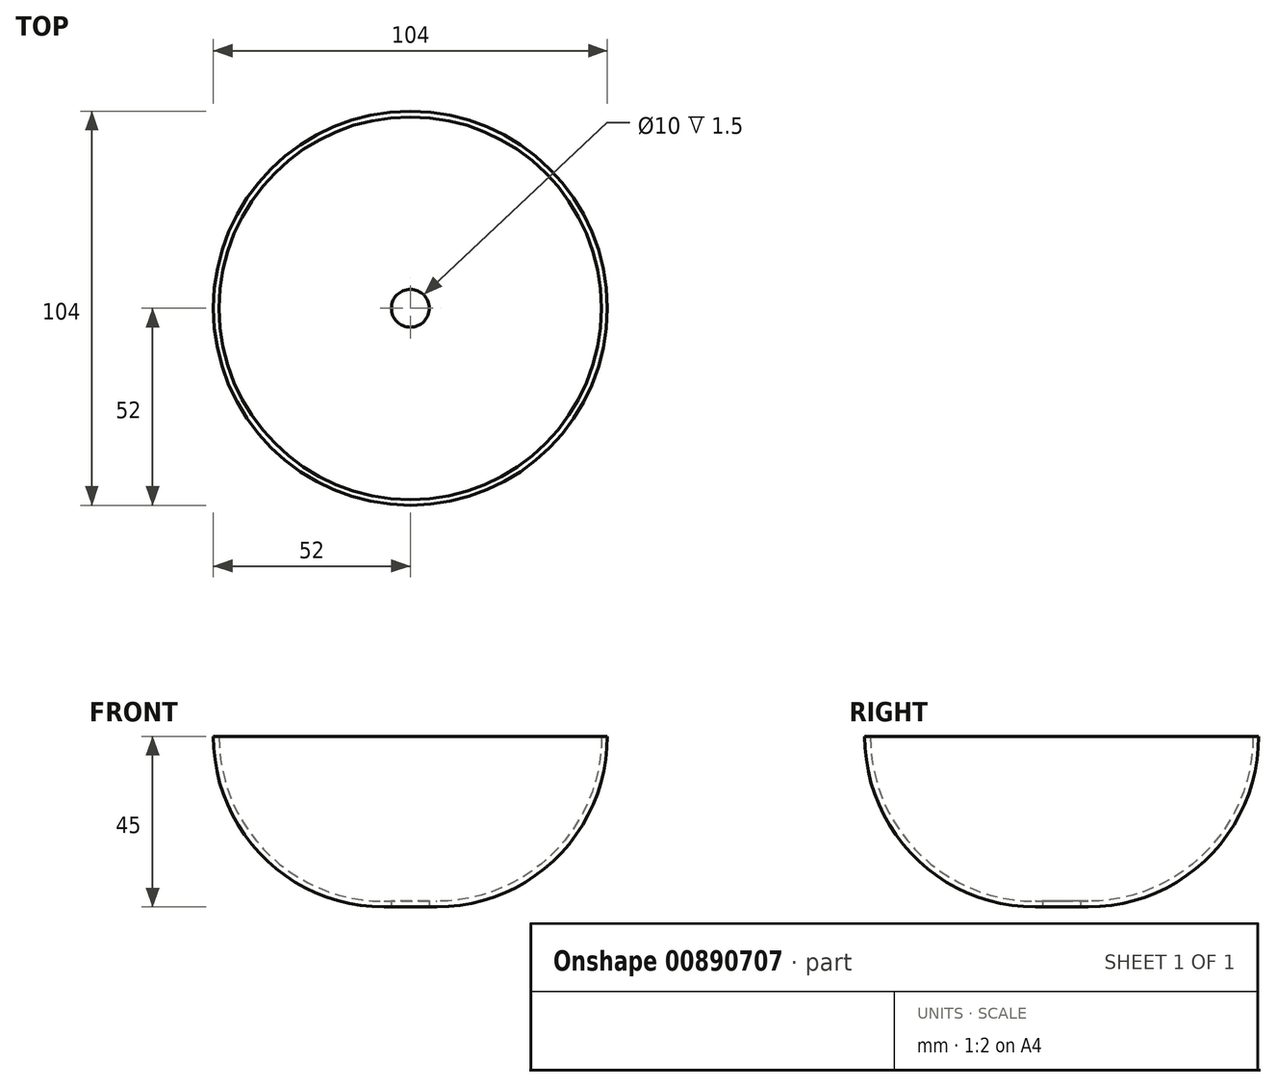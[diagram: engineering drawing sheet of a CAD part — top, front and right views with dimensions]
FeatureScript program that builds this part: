
annotation { "Feature Type Name" : "Feature", "Feature Type Description" : "" }
export const myFeature = defineFeature(function(context is Context, id is Id, definition is map)
    precondition{}
    {
        {
            var Q0;
            Q0=qCreatedBy(makeId("Front.planeOp"),FACE);
            var sketch = newSketch(context, id + "F0", { "sketchPlane" : qUnion([Q0])});
            skLineSegment(sketch, "E0", {"start": v(0, 0) * mm, "end": v(0, 45) * mm, "construction": true});
            skLineSegment(sketch, "E1", {"start": v(0, 0) * mm, "end": v(7, 0) * mm});
            skArc(sketch, "E2", {"start": v(7, 0) * mm, "mid": v(38.82, 13.18) * mm, "end": v(52, 45) * mm});
            skArc(sketch, "E3.0", {"start": v(7, 1.5) * mm, "mid": v(37.76, 14.24) * mm, "end": v(50.5, 45) * mm});
            skLineSegment(sketch, "E4", {"start": v(50.5, 45) * mm, "end": v(52, 45) * mm});
            skLineSegment(sketch, "E5", {"start": v(7, 1.5) * mm, "end": v(0, 1.5) * mm});
            skLineSegment(sketch, "E6", {"start": v(0, 1.5) * mm, "end": v(0, 0) * mm});
            skSolve(sketch);
        }
        {
            var Q0;
            Q0=makeQuery(id+"F0.imprint","IMPRINT",FACE,{"disambiguationData":[TD([[makeQuery(id+"F0.imprint","IMPRINT",EDGE,{"derivedFrom":sQuery(id+"F0.wireOp",EDGE,"E1")}),1.0]])]});
            var Q1;
            Q1=sQuery(id+"F0.wireOp",EDGE,"E0");
            revolve(context, id + "F1", {"surfaceOperationType" : NewSurfaceOperationType.NEW, "entities" : qUnion([Q0]), "axis" : qUnion([Q1]), "revolveType" : RevolveType.FULL});
        }
        {
            var Q0;
            Q0=qCreatedBy(makeId("Top.planeOp"),FACE);
            var sketch = newSketch(context, id + "F2", { "sketchPlane" : qUnion([Q0])});
            skCircle(sketch, "E7", {"center": v(0, 0) * mm, "radius": 5 * mm});
            skSolve(sketch);
        }
        {
            var Q0;
            Q0=makeQuery(id+"F2.imprint","IMPRINT",FACE,{"disambiguationData":[TD([[makeQuery(id+"F2.imprint","IMPRINT",EDGE,{"derivedFrom":sQuery(id+"F2.wireOp",EDGE,"E7")}),1.0]])]});
            extrude(context, id + "F3", {"entities" : qUnion([Q0]), "operationType" : NewBodyOperationType.REMOVE, "depth" : 1.5 * mm, "offsetDistance" : 25 * mm});
        }
    });
